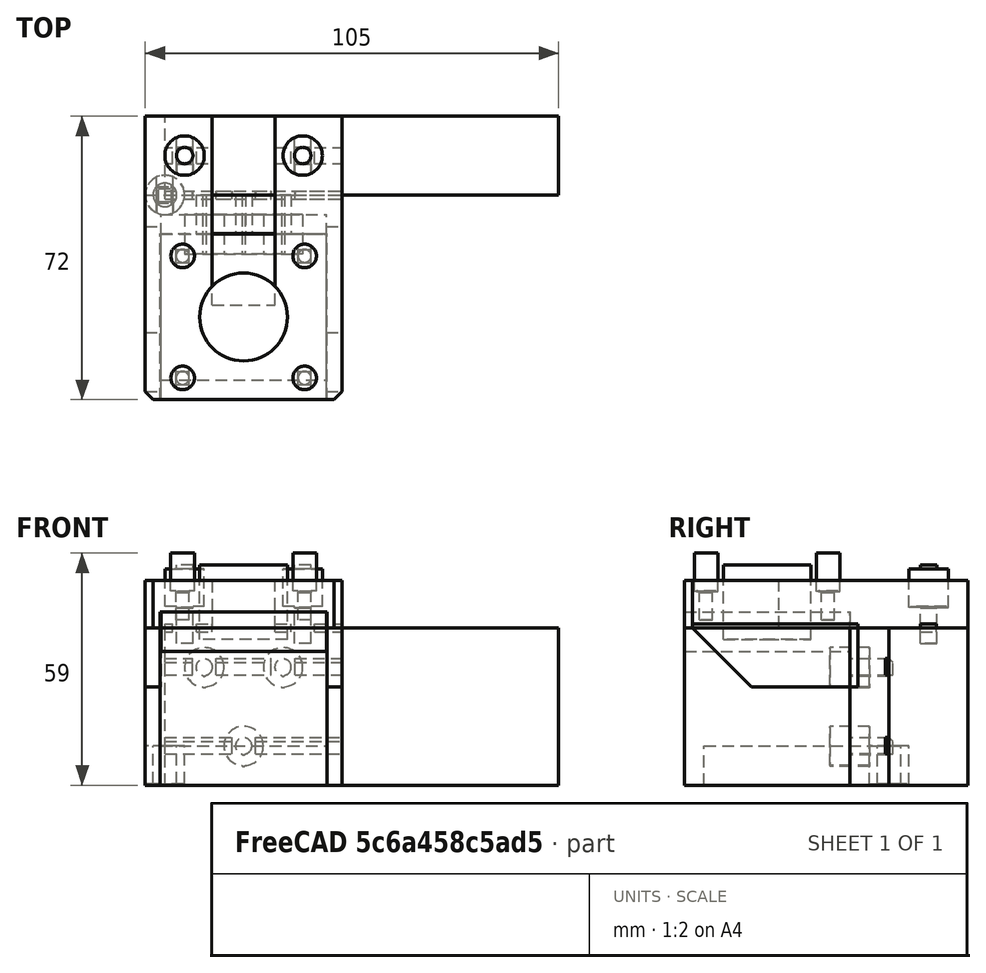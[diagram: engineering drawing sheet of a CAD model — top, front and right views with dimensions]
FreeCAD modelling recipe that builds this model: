
FCSTD DOCUMENT  (FreeCAD 0.18R14555 (Git shallow))
Label: motor-mount
License: All rights reserved
LicenseURL: http://en.wikipedia.org/wiki/All_rights_reserved
objects: Part::Box×24, Part::Cylinder×13, Part::MultiFuse×12, Part::Feature×11, Part::Chamfer×5, Part::Cut×3
note: 68 computed .brp shape members not serialized (recipe doc carries the construction recipe); baked Part::Feature solids carry a one-line shape summary decoded from their .brp

FEATURE [Part::Box] Box  label="frame"
  AttacherType = Attacher::AttachEngine3D
  Height = 40
  Length = 100
  Width = 20
FEATURE [Part::Box] Box001  label="Cube001"
  AttacherType = Attacher::AttachEngine3D
  Height = 12
  Length = 50
  Placement = pos=(-5,-52,40) rot=(0,0,1;0rad)
  Width = 72
FEATURE [Part::Box] Box002  label="motor"
  AttacherType = Attacher::AttachEngine3D
  Height = 10
  Length = 42
  Placement = pos=(-1,-47,0) rot=(0,0,1;0rad)
  Width = 42
FEATURE [Part::Box] Box003  label="Cube002"
  AttacherType = Attacher::AttachEngine3D
  Height = 40
  Length = 50
  Placement = pos=(-5,-10,0) rot=(0,0,1;0rad)
  Width = 10
FEATURE [Part::Box] Box004  label="Cube003"
  AttacherType = Attacher::AttachEngine3D
  Height = 16
  Length = 4
  Placement = pos=(-5,-47,25) rot=(0,0,1;0rad)
  Width = 42
FEATURE [Part::Box] Box005  label="Cube004"
  AttacherType = Attacher::AttachEngine3D
  Height = 16
  Length = 4
  Placement = pos=(41,-47,25) rot=(0,0,1;0rad)
  Width = 42
FEATURE [Part::Box] Box006  label="Cube005"
  AttacherType = Attacher::AttachEngine3D
  Height = 40
  Length = 5
  Placement = pos=(-5,0,0) rot=(0,0,1;0rad)
  Width = 20
FEATURE [Part::Cylinder] Cylinder
  Angle = 360
  AttacherType = Attacher::AttachEngine3D
  Height = 19
  Placement = pos=(20,-31,37) rot=(0,0,1;0rad)
  Radius = 11.15
FEATURE [Part::Cylinder] Cylinder001
  Angle = 360
  AttacherType = Attacher::AttachEngine3D
  Height = 10
  Placement = pos=(4.5,-10.5,37) rot=(0,0,1;0rad)
  Radius = 1.65
FEATURE [Part::Cylinder] Cylinder002
  Angle = 360
  AttacherType = Attacher::AttachEngine3D
  Height = 10
  Placement = pos=(35.5,-10.5,37) rot=(0,0,1;0rad)
  Radius = 1.65
FEATURE [Part::Cylinder] Cylinder003
  Angle = 360
  AttacherType = Attacher::AttachEngine3D
  Height = 10
  Placement = pos=(4.5,-41.5,37) rot=(0,0,1;0rad)
  Radius = 1.65
FEATURE [Part::Cylinder] Cylinder004
  Angle = 360
  AttacherType = Attacher::AttachEngine3D
  Height = 10
  Placement = pos=(35.5,-41.5,37) rot=(0,0,1;0rad)
  Radius = 1.65
FEATURE [Part::MultiFuse] Fusion001
  Placement = pos=(0,-5,5) rot=(0,0,1;0rad)
  Shapes = -> [Cylinder004,Cylinder002,Cylinder003,Cylinder001]
FEATURE [Part::Cylinder] Cylinder005
  Angle = 360
  AttacherType = Attacher::AttachEngine3D
  Height = 20
  Placement = pos=(5,0,0) rot=(0,0,1;0rad)
  Radius = 2.1
FEATURE [Part::Cylinder] Cylinder006
  Angle = 360
  AttacherType = Attacher::AttachEngine3D
  Height = 20
  Placement = pos=(35,0,0) rot=(0,0,1;0rad)
  Radius = 2.1
FEATURE [Part::Cylinder] Cylinder007
  Angle = 360
  AttacherType = Attacher::AttachEngine3D
  Height = 10
  Radius = 5
FEATURE [Part::Box] Box007  label="Cube"
  AttacherType = Attacher::AttachEngine3D
  Height = 0.2
  Length = 10
  Placement = pos=(-5,2.1,0) rot=(0,0,1;0rad)
  Width = 10
FEATURE [Part::Box] Box008  label="Cube006"
  AttacherType = Attacher::AttachEngine3D
  Height = 0.2
  Length = 10
  Placement = pos=(-5,-12.1,0) rot=(0,0,1;0rad)
  Width = 10
FEATURE [Part::Box] Box009  label="Cube007"
  AttacherType = Attacher::AttachEngine3D
  Height = 0.4
  Length = 10
  Placement = pos=(-12.1,-5,0) rot=(0,0,1;0rad)
  Width = 10
FEATURE [Part::Box] Box010  label="Cube008"
  AttacherType = Attacher::AttachEngine3D
  Height = 0.4
  Length = 10
  Placement = pos=(2.1,-5,0) rot=(0,0,1;0rad)
  Width = 10
FEATURE [Part::MultiFuse] Fusion003
  Shapes = -> [Box007,Box010,Box009,Box008]
FEATURE [Part::Cut] Cut003  label="m4-slot"
  Base = -> Cylinder007
  Tool = -> Fusion003
FEATURE [Part::Cylinder] Cylinder008
  Angle = 360
  AttacherType = Attacher::AttachEngine3D
  Height = 10
  Radius = 3
FEATURE [Part::Box] Box011  label="Cube009"
  AttacherType = Attacher::AttachEngine3D
  Height = 0.2
  Length = 10
  Placement = pos=(-5,1.65,0) rot=(0,0,1;0rad)
  Width = 10
FEATURE [Part::Box] Box012  label="Cube010"
  AttacherType = Attacher::AttachEngine3D
  Height = 0.2
  Length = 10
  Placement = pos=(-5,-11.65,0) rot=(0,0,1;0rad)
  Width = 10
FEATURE [Part::Box] Box013  label="Cube011"
  AttacherType = Attacher::AttachEngine3D
  Height = 0.4
  Length = 10
  Placement = pos=(-11.65,-5,0) rot=(0,0,1;0rad)
  Width = 10
FEATURE [Part::Box] Box014  label="Cube012"
  AttacherType = Attacher::AttachEngine3D
  Height = 0.4
  Length = 10
  Placement = pos=(1.65,-5,0) rot=(0,0,1;0rad)
  Width = 10
FEATURE [Part::MultiFuse] Fusion004
  Shapes = -> [Box011,Box013,Box012,Box014]
FEATURE [Part::Cut] Cut004  label="m3-slot"
  Base = -> Cylinder008
  Tool = -> Fusion004
FEATURE [Part::Feature] Cut003001  label="m4-slot001"
  Placement = pos=(5,10,43) rot=(0,0,1;0rad)
  shape: bbox 10 x 10 x 10 mm, 11 faces (baked)
FEATURE [Part::Feature] Cut003002  label="m4-slot002"
  Placement = pos=(35,10,43) rot=(0,0,1;0rad)
  shape: bbox 10 x 10 x 10 mm, 11 faces (baked)
FEATURE [Part::Feature] Cut004001  label="m3-slot001"
  Placement = pos=(4.5,-10.5,0) rot=(0,0,1;0rad)
  shape: bbox 6 x 6 x 10 mm, 11 faces (baked)
FEATURE [Part::Feature] Cut004002  label="m3-slot002"
  Placement = pos=(35.5,-10.5,0) rot=(0,0,1;0rad)
  shape: bbox 6 x 6 x 10 mm, 11 faces (baked)
FEATURE [Part::Feature] Cut004003  label="m3-slot003"
  Placement = pos=(4.5,-41.5,0) rot=(0,0,1;0rad)
  shape: bbox 6 x 6 x 10 mm, 11 faces (baked)
FEATURE [Part::Feature] Cut004004  label="m3-slot004"
  Placement = pos=(35.5,-41.5,0) rot=(0,0,1;0rad)
  shape: bbox 6 x 6 x 10 mm, 11 faces (baked)
FEATURE [Part::MultiFuse] Fusion005
  Placement = pos=(0,-5,49) rot=(0,0,1;0rad)
  Shapes = -> [Cut004004,Cut004001,Cut004002,Cut004003]
FEATURE [Part::Cylinder] Cylinder009
  Angle = 360
  AttacherType = Attacher::AttachEngine3D
  Height = 10
  Placement = pos=(10,1.8e-15,8.2) rot=(1,0,0;1.5708rad)
  Radius = 0.5
FEATURE [Part::Cylinder] Cylinder014
  Angle = 360
  AttacherType = Attacher::AttachEngine3D
  Height = 10
  Placement = pos=(10,1.2e-15,5.3) rot=(1,0,0;1.5708rad)
  Radius = 0.5
FEATURE [Part::Cylinder] Cylinder015
  Angle = 360
  AttacherType = Attacher::AttachEngine3D
  Height = 10
  Placement = pos=(10,2.2e-15,10) rot=(1,0,0;1.5708rad)
  Radius = 5
FEATURE [Part::Box] Box015  label="Cube013"
  AttacherType = Attacher::AttachEngine3D
  Height = 4.2
  Length = 17
  Placement = pos=(0,-1,8) rot=(0,0,1;0rad)
  Width = 2
FEATURE [Part::Box] Box018  label="Cube016"
  AttacherType = Attacher::AttachEngine3D
  Height = 2
  Length = 2
  Placement = pos=(0,8,39) rot=(0,0,1;0rad)
  Width = 4
FEATURE [Part::Box] Box021  label="Cube019"
  AttacherType = Attacher::AttachEngine3D
  Height = 4.2
  Length = 22
  Placement = pos=(23,-1,8) rot=(0,0,1;0rad)
  Width = 2
FEATURE [Part::Box] Box022  label="middle-cut"
  AttacherType = Attacher::AttachEngine3D
  Height = 12
  Length = 16
  Placement = pos=(12,-28,40) rot=(0,0,1;0rad)
  Width = 49
FEATURE [Part::MultiFuse] Fusion011
  Placement = pos=(0,0,2) rot=(0,0,1;0rad)
  Shapes = -> [Cut003001,Cut003002]
FEATURE [Part::Box] Box023  label="Cube021"
  AttacherType = Attacher::AttachEngine3D
  Height = 2
  Length = 4
  Placement = pos=(8,8,39) rot=(0,0,1;0rad)
  Width = 4
FEATURE [Part::Box] Box024  label="Cube022"
  AttacherType = Attacher::AttachEngine3D
  Height = 2
  Length = 4
  Placement = pos=(28,8,39) rot=(0,0,1;0rad)
  Width = 4
FEATURE [Part::Box] Box025  label="Cube023"
  AttacherType = Attacher::AttachEngine3D
  Height = 2
  Length = 7
  Placement = pos=(38,8,39) rot=(0,0,1;0rad)
  Width = 4
FEATURE [Part::Box] Box026  label="Cube024"
  AttacherType = Attacher::AttachEngine3D
  Height = 10
  Length = 42
  Placement = pos=(-1,-52,34) rot=(0,0,1;0rad)
  Width = 42
FEATURE [Part::MultiFuse] Fusion
  Placement = pos=(0,10,36) rot=(0,0,1;0rad)
  Shapes = -> [Cylinder006,Cylinder005]
FEATURE [Part::Chamfer] Chamfer
  Base = -> Box004
  Edges = 1 edges r=15: [Edge9]
FEATURE [Part::Chamfer] Chamfer006
  Base = -> Box005
  Edges = 1 edges r=15: [Edge9]
FEATURE [Part::Feature] Fusion014001  label="Fusion016"
  Placement = pos=(0,0,20) rot=(0,0,1;0rad)
  shape: bbox 24.2 x 10 x 4.4 mm, 18 faces, 2 solids (baked)
FEATURE [Part::Feature] Fusion013001  label="Fusion017"
  Placement = pos=(0,0,20) rot=(0,0,1;0rad)
  shape: bbox 30 x 10 x 10.2 mm, 18 faces, 2 solids (baked)
FEATURE [Part::Feature] Chamfer003001  label="Chamfer008"
  Placement = pos=(0,0,20) rot=(0,0,1;0rad)
  shape: bbox 12 x 2 x 4.2 mm, 7 faces (baked)
FEATURE [Part::Feature] Chamfer004001  label="Chamfer010"
  Placement = pos=(0,0,20) rot=(0,0,1;0rad)
  shape: bbox 14 x 2 x 4.2 mm, 7 faces (baked)
FEATURE [Part::Feature] Chamfer005001  label="Chamfer009"
  Placement = pos=(0,0,20) rot=(0,0,1;0rad)
  shape: bbox 7 x 2 x 4.2 mm, 7 faces (baked)
FEATURE [Part::MultiFuse] Fusion014008
  Placement = pos=(0,-3,0) rot=(0,0,1;0rad)
  Shapes = -> [Chamfer,Chamfer006]
FEATURE [Part::Chamfer] Chamfer005002
  Base = -> Box001
  Edges = 2 edges r=2: [Edge1,Edge5]
FEATURE [Part::Box] Box027  label="Cube025"
  AttacherType = Attacher::AttachEngine3D
  Height = 44
  Length = 42.4
  Placement = pos=(-1.2,-52,0) rot=(0,0,1;0rad)
  Width = 42.2
FEATURE [Part::MultiFuse] Fusion014015
  Shapes = -> [Box018,Box023,Box024,Box025]
FEATURE [Part::MultiFuse] Fusion014017
  Shapes = -> [Fusion005,Fusion001,Fusion011,Fusion]
FEATURE [Part::Cut] Cut
  Base = -> Chamfer005002
  Tool = -> Box022
FEATURE [Part::Cylinder] Cylinder011
  Angle = 360
  AttacherType = Attacher::AttachEngine3D
  Height = 10
  Placement = pos=(10,2.2e-15,10) rot=(1,0,0;1.5708rad)
  Radius = 2.1
FEATURE [Part::MultiFuse] Fusion014018
  Placement = pos=(10,0,0) rot=(0,0,1;0rad)
  Shapes = -> [Cylinder009,Cylinder011]
FEATURE [Part::Chamfer] Chamfer005003
  Base = -> Box021
  Edges = 1 edges r=1: [Edge12]
FEATURE [Part::Chamfer] Chamfer005004
  Base = -> Box015
  Edges = 1 edges r=1: [Edge12]
FEATURE [Part::MultiFuse] Fusion014019
  Placement = pos=(10,-3,0) rot=(0,0,1;0rad)
  Shapes = -> [Cylinder014,Cylinder015]
FEATURE [Part::MultiFuse] Fusion014020
  Placement = pos=(0,-2,0) rot=(0,0,1;0rad)
  Shapes = -> [Fusion014019,Fusion013001]
